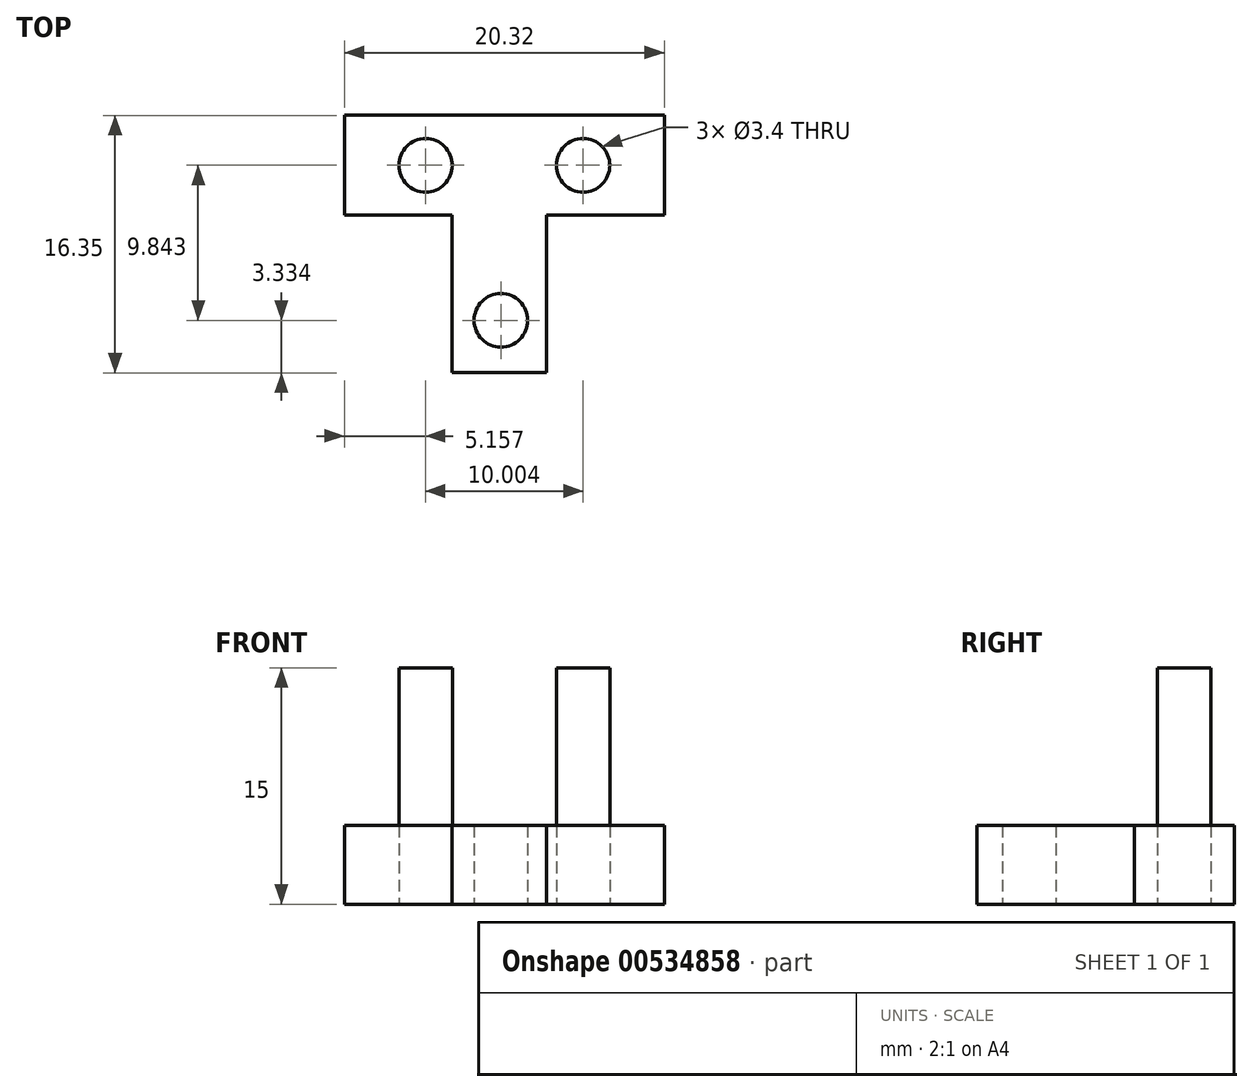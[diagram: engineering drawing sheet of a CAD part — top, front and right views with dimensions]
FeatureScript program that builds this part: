
annotation { "Feature Type Name" : "Feature", "Feature Type Description" : "" }
export const myFeature = defineFeature(function(context is Context, id is Id, definition is map)
    precondition{}
    {
        {
            var Q0;
            Q0=qCreatedBy(makeId("Top.planeOp"),FACE);
            var sketch = newSketch(context, id + "F0", { "sketchPlane" : qUnion([Q0])});
            skCircle(sketch, "E0", {"center": v(-28.5, 21.3) * mm, "radius": 1.7 * mm});
            skCircle(sketch, "E1", {"center": v(-18.49, 21.3) * mm, "radius": 1.7 * mm});
            skLineSegment(sketch, "E2", {"start": v(-26.8, 21.3) * mm, "end": v(-20.19, 21.3) * mm});
            skPoint(sketch, "E3", {"position": v(-23.5, 21.3) * mm});
            skLineSegment(sketch, "E4.bottom", {"start": v(-13.33, 24.47) * mm, "end": v(-33.65, 24.47) * mm});
            skLineSegment(sketch, "E4.top", {"start": v(-13.33, 18.12) * mm, "end": v(-33.65, 18.12) * mm});
            skLineSegment(sketch, "E4.left", {"start": v(-13.33, 24.47) * mm, "end": v(-13.33, 18.12) * mm});
            skLineSegment(sketch, "E4.right", {"start": v(-33.65, 24.47) * mm, "end": v(-33.65, 18.12) * mm});
            skLineSegment(sketch, "E5.top", {"start": v(-26.82, 8.12) * mm, "end": v(-20.82, 8.12) * mm});
            skLineSegment(sketch, "E5.left", {"start": v(-26.82, 18.12) * mm, "end": v(-26.82, 8.12) * mm});
            skLineSegment(sketch, "E5.right", {"start": v(-20.82, 18.12) * mm, "end": v(-20.82, 8.12) * mm});
            skPoint(sketch, "E6.positionSnap1", {"position": v(-23.5, 18.12) * mm});
            skCircle(sketch, "E7", {"center": v(-23.7, 11.45) * mm, "radius": 1.7 * mm});
            skSolve(sketch);
        }
        {
            var Q0;
            Q0=qSketchRegion(id+"F0",true);
            extrude(context, id + "F1", {"entities" : qUnion([Q0]), "depth" : 5 * mm, "offsetDistance" : 25.4 * mm});
        }
        {
            var Q0;
            Q0=makeQuery(id+"F1.opExtrude","CAP_FACE",FACE,{"disambiguationData":[OSD([sQuery(id+"F0.wireOp",EDGE,"E0"),sQuery(id+"F0.wireOp",EDGE,"E1"),sQuery(id+"F0.wireOp",EDGE,"E4.bottom"),sQuery(id+"F0.wireOp",EDGE,"E4.top"),sQuery(id+"F0.wireOp",EDGE,"E4.left"),sQuery(id+"F0.wireOp",EDGE,"E4.right"),sQuery(id+"F0.wireOp",EDGE,"E5.top"),sQuery(id+"F0.wireOp",EDGE,"E5.left"),sQuery(id+"F0.wireOp",EDGE,"E5.right"),sQuery(id+"F0.wireOp",EDGE,"E7")])],"isStart":true});
            var sketch = newSketch(context, id + "F2", { "sketchPlane" : qUnion([Q0])});
            skCircle(sketch, "E8", {"center": v(-28.5, -21.3) * mm, "radius": 1.7 * mm});
            skPoint(sketch, "E8.first.point", {"position": v(-28.53, -19.6) * mm});
            skPoint(sketch, "E8.second.point", {"position": v(-28.5, -23) * mm});
            skPoint(sketch, "E8.third.point", {"position": v(-27.38, -22.58) * mm});
            skSolve(sketch);
        }
        {
            var Q0;
            Q0=qSketchRegion(id+"F2",true);
            extrude(context, id + "F3", {"entities" : qUnion([Q0]), "oppositeDirection" : true, "depth" : 15 * mm, "offsetDistance" : 25.4 * mm});
        }
        {
            var Q0;
            Q0=makeQuery(id+"F1.opExtrude","CAP_FACE",FACE,{"disambiguationData":[OSD([sQuery(id+"F0.wireOp",EDGE,"E0"),sQuery(id+"F0.wireOp",EDGE,"E1"),sQuery(id+"F0.wireOp",EDGE,"E4.bottom"),sQuery(id+"F0.wireOp",EDGE,"E4.top"),sQuery(id+"F0.wireOp",EDGE,"E4.left"),sQuery(id+"F0.wireOp",EDGE,"E4.right"),sQuery(id+"F0.wireOp",EDGE,"E5.top"),sQuery(id+"F0.wireOp",EDGE,"E5.left"),sQuery(id+"F0.wireOp",EDGE,"E5.right"),sQuery(id+"F0.wireOp",EDGE,"E7")])],"isStart":true});
            var sketch = newSketch(context, id + "F4", { "sketchPlane" : qUnion([Q0])});
            skCircle(sketch, "E9", {"center": v(-18.49, -21.3) * mm, "radius": 1.7 * mm});
            skPoint(sketch, "E9.first.point", {"position": v(-18.58, -19.6) * mm});
            skPoint(sketch, "E9.second.point", {"position": v(-18.47, -23) * mm});
            skPoint(sketch, "E9.third.point", {"position": v(-16.8, -21.56) * mm});
            skSolve(sketch);
        }
        {
            var Q0;
            Q0=qSketchRegion(id+"F4",true);
            extrude(context, id + "F5", {"entities" : qUnion([Q0]), "oppositeDirection" : true, "depth" : 15 * mm, "offsetDistance" : 25.4 * mm});
        }
    });
